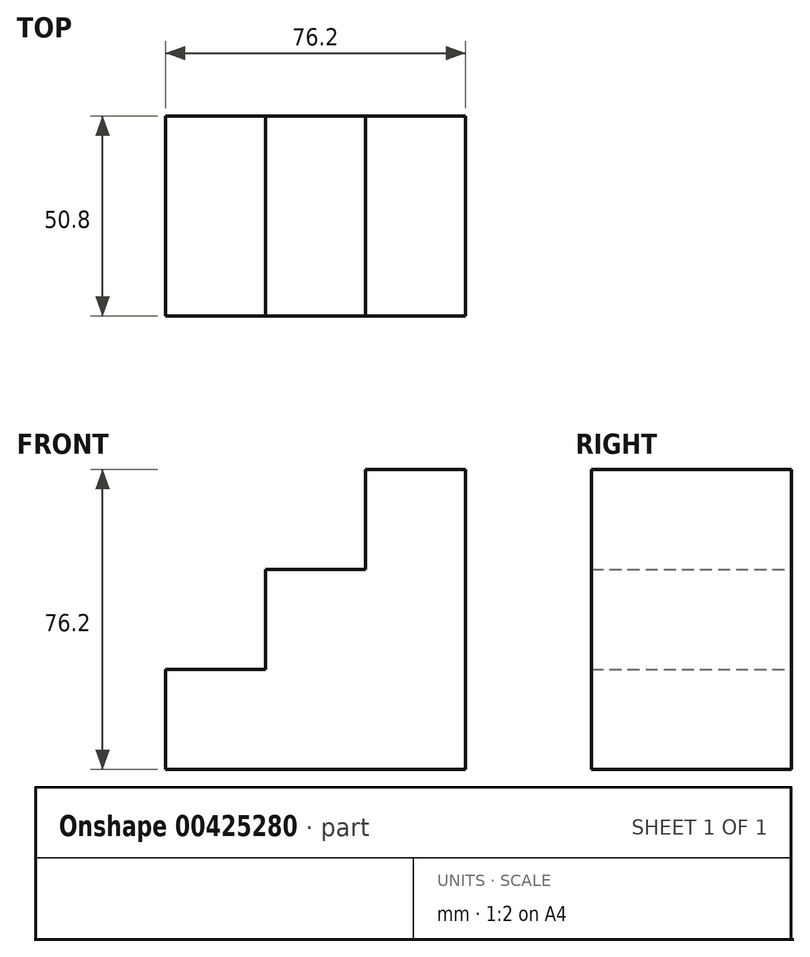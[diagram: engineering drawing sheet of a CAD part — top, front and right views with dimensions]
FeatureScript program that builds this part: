
annotation { "Feature Type Name" : "Feature", "Feature Type Description" : "" }
export const myFeature = defineFeature(function(context is Context, id is Id, definition is map)
    precondition{}
    {
        {
            var Q0;
            Q0=qCreatedBy(makeId("Front.planeOp"),FACE);
            var sketch = newSketch(context, id + "F0", { "sketchPlane" : qUnion([Q0])});
            skLineSegment(sketch, "E0", {"start": v(17.2, 70.66) * mm, "end": v(17.2, -5.54) * mm});
            skLineSegment(sketch, "E1", {"start": v(17.2, 70.66) * mm, "end": v(-8.2, 70.66) * mm});
            skLineSegment(sketch, "E2", {"start": v(-8.2, 70.66) * mm, "end": v(-8.2, 45.26) * mm});
            skLineSegment(sketch, "E3", {"start": v(-8.2, 45.26) * mm, "end": v(-33.6, 45.26) * mm});
            skLineSegment(sketch, "E4", {"start": v(-33.6, 45.26) * mm, "end": v(-33.6, 19.86) * mm});
            skLineSegment(sketch, "E5", {"start": v(-33.6, 19.86) * mm, "end": v(-59, 19.86) * mm});
            skLineSegment(sketch, "E6", {"start": v(-59, 19.86) * mm, "end": v(-59, -5.54) * mm});
            skLineSegment(sketch, "E7", {"start": v(-59, -5.54) * mm, "end": v(17.2, -5.54) * mm});
            skSolve(sketch);
        }
        {
            var Q0;
            Q0 = qSketchRegion(id + "F0", true);
            extrude(context, id + "F1", {"entities" : qUnion([Q0]), "depth" : 50.8 * mm});
        }
    });
